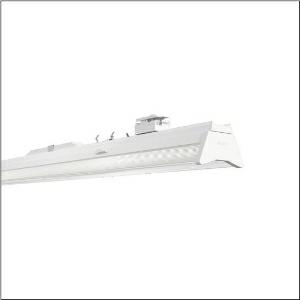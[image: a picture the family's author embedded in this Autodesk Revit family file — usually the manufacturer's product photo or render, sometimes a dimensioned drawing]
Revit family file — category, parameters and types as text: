
# Revit family: licross_r__11_performance_mo_51tm16dn445g_758e
name_source: partatom
category: Lighting Fixtures
units: mm (PartAtom-declared; Revit-internal decimal feet)

## family parameters
Cut with Voids When Loaded = No
Host = Face
Light Source = No
Part Type = Normal
Room Calculation Point = No
Round Connector Dimension = Use Diameter
Shared = No

## types (1)
- --- (1 x LED, 4520 lm, 24.3 W, 4000K)
    Apparent Load = 24 VA
    CIE Flux Codes = 66 88 96 79 100
    Color Rendering = 80
    Color Temperature = 4000K
    Default Elevation = 1800 mm
    Description = Licross® 11 Performance MO, luminaire insert, of sheet steel, galvanised, coil coated, white, length: 1.500mm, width: 120mm, height: 123mm, LED rated luminous flux: 4.520lm, light colour: 840, control gear: DALI 2, with plug, 5-pole, with phase selection, mains connection: 220..240V, AC, 50/60Hz, rated input power: 24W, internal wiring halogen-free, primary light control with lens, of plastic, primary optical cover: cover, of PMMA, CAT 2 (L<= 3000cd/m²), light emission: direct/indirect distribution, primary light characteristic: symmetric, protection rating (complete): IP40, insulation class (complete): insulation class I (protective earthing), certification: CE, ENEC, VDE, UKCA, protection symbol: D if used in an environment without relevant dust loads with corresponding accessories, impact resistance: IK06, permissible ambient temperature for indoor applications: -25..+45°C, corresponds to IFS (International Featured Standards) requirements for safety and quality in the food industry, reducing of maximum allowable ambient temperature of 5°C with ceiling mounting, LABS conformity tested according to VDMA 24364:2018-05, packaging unit: 1 piece
    Height = 114 mm
    Lamp = 1 x LED
    Lamp Light Flux = 4520 lm
    Lamp Power = 24.3 W
    Lamp count = 1
    Length = 1500 mm
    Luminous efficacy = 186 lm/W
    Manufacturer = Siteco
    ModVariant = No
    Model = 51TM16DN445G
    Mounting Place = Ceiling
    Mounting Type = Pendant
    Number of Poles = 1
    OnlyDefault = Yes
    Power Factor = 1
    Product Name = Licross® 11 Performance MO
    Product group = luminaire insert | ceiling pendant
    ProductGroupID = 902
    Protection Class = Protection class I
    Protection Degree = IP 40
    RLX_Detail_Level = 1
    RLX_Emergency_Light_Flux = 0 lm
    RLX_Emergency_Type = 0
    RLX_Emergency_Type_DB = No
    RlxData = <blob elided: 33881 chars, md5=2bd25c64>
    Socket = socket
    Standby Power = 0 W
    System Light Flux = 4520 lm
    System Power = 24 W
    Type Comments = factory setting: luminous flux: 100 % | dim-lin: 254 | 161 mA
    Type Image = l_1256138.jpg
    URL = http://relux.com
    VarID = @adj_070047
    Voltage = 0 V
    Weight = 0.00 kg
    Width = 120 mm

## geometry (parser evidence)
native form markers: Blend x4, Sweep x10
no freeform markers — native parametric forms only
